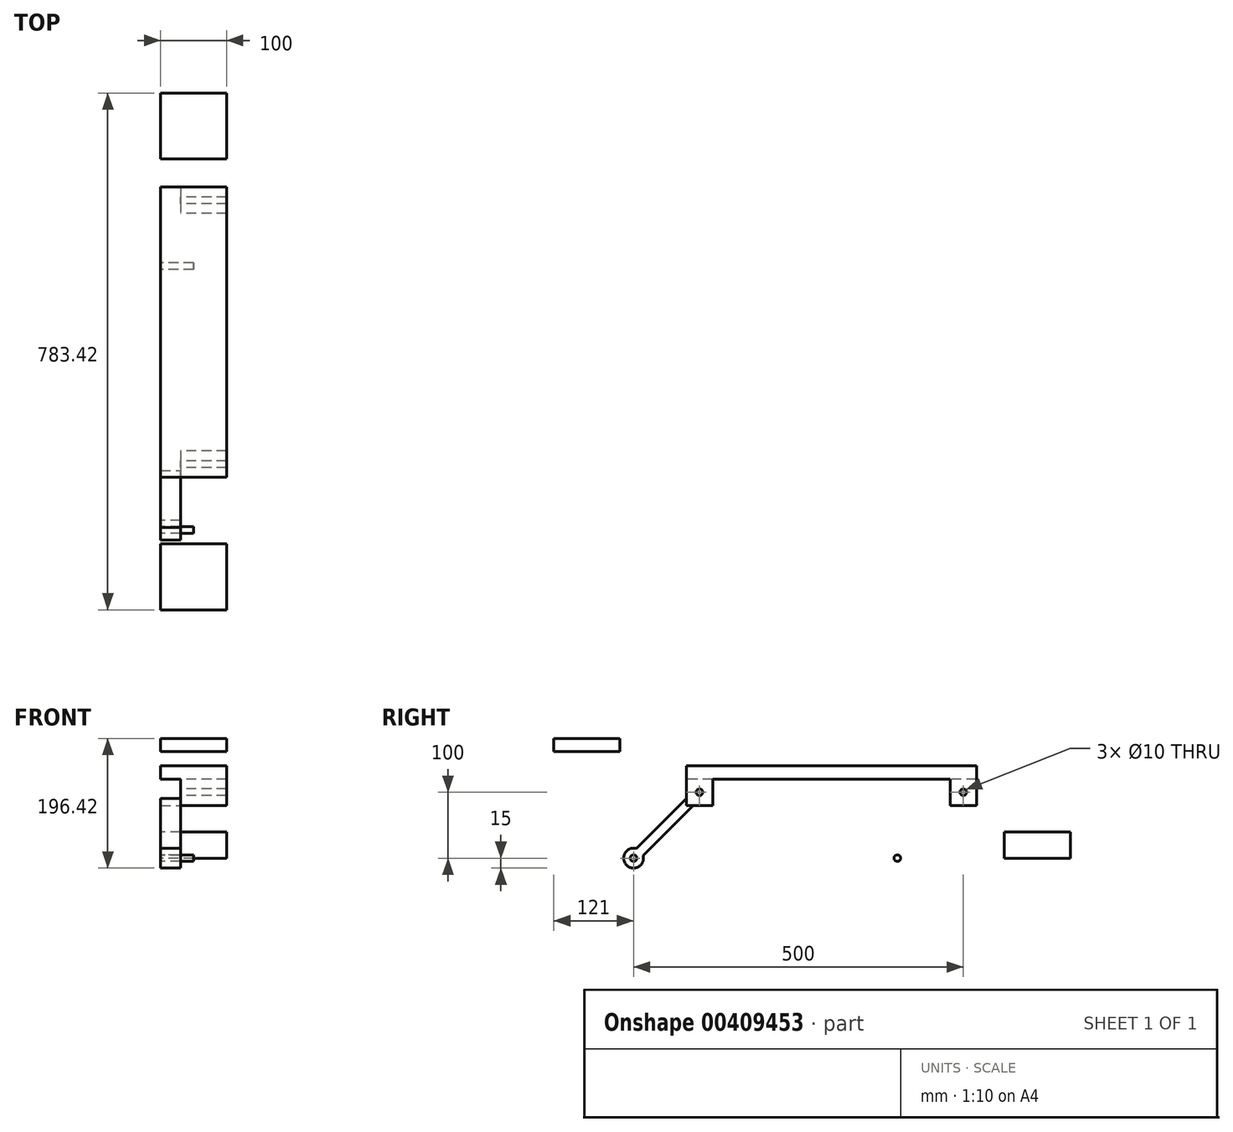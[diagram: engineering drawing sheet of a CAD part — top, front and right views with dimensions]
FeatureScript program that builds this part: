
annotation { "Feature Type Name" : "Feature", "Feature Type Description" : "" }
export const myFeature = defineFeature(function(context is Context, id is Id, definition is map)
    precondition{}
    {
        {
            var Q0;
            Q0=qCreatedBy(makeId("Right.planeOp"),FACE);
            var sketch = newSketch(context, id + "F0", { "sketchPlane" : qUnion([Q0])});
            skLineSegment(sketch, "E0", {"start": v(0, 0) * mm, "end": v(100, 100) * mm, "construction": true});
            skLineSegment(sketch, "E1", {"start": v(100, 100) * mm, "end": v(500, 100) * mm, "construction": true});
            skLineSegment(sketch, "E2", {"start": v(500, 100) * mm, "end": v(400, 0) * mm, "construction": true});
            skLineSegment(sketch, "E3", {"start": v(400, 0) * mm, "end": v(0, 0) * mm, "construction": true});
            skCircle(sketch, "E4", {"center": v(100, 100) * mm, "radius": 5 * mm});
            skCircle(sketch, "E5", {"center": v(500, 100) * mm, "radius": 5 * mm});
            skLineSegment(sketch, "E6.bottom", {"start": v(120, 80) * mm, "end": v(80, 80) * mm});
            skLineSegment(sketch, "E6.top", {"start": v(120, 120) * mm, "end": v(80, 120) * mm});
            skLineSegment(sketch, "E6.left", {"start": v(120, 80) * mm, "end": v(120, 120) * mm});
            skLineSegment(sketch, "E6.right", {"start": v(80, 80) * mm, "end": v(80, 120) * mm});
            skLineSegment(sketch, "E7.bottom", {"start": v(520, 80) * mm, "end": v(480, 80) * mm});
            skLineSegment(sketch, "E7.top", {"start": v(520, 120) * mm, "end": v(480, 120) * mm});
            skLineSegment(sketch, "E7.left", {"start": v(520, 80) * mm, "end": v(520, 120) * mm});
            skLineSegment(sketch, "E7.right", {"start": v(480, 80) * mm, "end": v(480, 120) * mm});
            skLineSegment(sketch, "E8.bottom", {"start": v(80, 120) * mm, "end": v(520, 120) * mm});
            skLineSegment(sketch, "E8.top", {"start": v(80, 140) * mm, "end": v(520, 140) * mm});
            skLineSegment(sketch, "E8.left", {"start": v(80, 120) * mm, "end": v(80, 140) * mm});
            skLineSegment(sketch, "E8.right", {"start": v(520, 120) * mm, "end": v(520, 140) * mm});
            skCircle(sketch, "E9", {"center": v(100, 100) * mm, "radius": 15 * mm});
            skCircle(sketch, "E10", {"center": v(0, 0) * mm, "radius": 15 * mm});
            skLineSegment(sketch, "E11", {"start": v(3.88, 14.49) * mm, "end": v(85.51, 96.12) * mm});
            skLineSegment(sketch, "E12.MirrorCS", {"start": v(14.49, 3.88) * mm, "end": v(96.12, 85.51) * mm});
            skCircle(sketch, "E13", {"center": v(0, 0) * mm, "radius": 5 * mm});
            skCircle(sketch, "E14", {"center": v(400, 0) * mm, "radius": 141.42 * mm, "construction": true});
            skLineSegment(sketch, "E15", {"start": v(400, 0) * mm, "end": v(949.52, 0) * mm, "construction": true});
            skLineSegment(sketch, "E16.bottom", {"start": v(562.42, 0) * mm, "end": v(662.42, 0) * mm});
            skLineSegment(sketch, "E16.top", {"start": v(562.42, 40) * mm, "end": v(662.42, 40) * mm});
            skLineSegment(sketch, "E16.left", {"start": v(562.42, 0) * mm, "end": v(562.42, 40) * mm});
            skLineSegment(sketch, "E16.right", {"start": v(662.42, 0) * mm, "end": v(662.42, 40) * mm});
            skCircle(sketch, "E17", {"center": v(0, 0) * mm, "radius": 141.42 * mm, "construction": true});
            skLineSegment(sketch, "E18", {"start": v(0, 0) * mm, "end": v(0, 382.71) * mm, "construction": true});
            skLineSegment(sketch, "E19.bottom", {"start": v(-21, 181.42) * mm, "end": v(-121, 181.42) * mm});
            skLineSegment(sketch, "E19.top", {"start": v(-21, 161.42) * mm, "end": v(-121, 161.42) * mm});
            skLineSegment(sketch, "E19.left", {"start": v(-21, 181.42) * mm, "end": v(-21, 161.42) * mm});
            skLineSegment(sketch, "E19.right", {"start": v(-121, 181.42) * mm, "end": v(-121, 161.42) * mm});
            skCircle(sketch, "E20", {"center": v(400, 0) * mm, "radius": 5 * mm});
            skSolve(sketch);
        }
        {
            var Q0;
            {var subQ1=sQuery(id+"F0.wireOp",EDGE,"E6.left");Q0=makeQuery(id+"F0.imprint","IMPRINT",FACE,{"disambiguationData":[TD([[makeQuery(id+"F0.imprint","IMPRINT",EDGE,{"derivedFrom":subQ1}),1.0]])]});}
            var Q1;
            {var subQ3=sQuery(id+"F0.wireOp",EDGE,"E6.right");var subQ7=sQuery(id+"F0.wireOp",EDGE,"E6.bottom");var subQ8=makeQuery(id+"F0.imprint","INTERSECT",VERTEX,{"derivedFrom":[subQ7,subQ3]});Q1=makeQuery(id+"F0.imprint","IMPRINT",FACE,{"disambiguationData":[TD([[makeQuery(id+"F0.imprint","IMPRINT",EDGE,{"disambiguationData":[TD([[subQ8,1.0]])],"derivedFrom":subQ7}),-1.0]])]});}
            var Q2;
            Q2=makeQuery(id+"F0.imprint","IMPRINT",FACE,{"disambiguationData":[TD([[makeQuery(id+"F0.imprint","IMPRINT",EDGE,{"derivedFrom":sQuery(id+"F0.wireOp",EDGE,"E4")}),-1.0]])]});
            var Q3;
            Q3=makeQuery(id+"F0.imprint","IMPRINT",FACE,{"disambiguationData":[TD([[makeQuery(id+"F0.imprint","IMPRINT",EDGE,{"derivedFrom":sQuery(id+"F0.wireOp",EDGE,"E8.top")}),-1.0]])]});
            var Q4;
            Q4=makeQuery(id+"F0.imprint","IMPRINT",FACE,{"disambiguationData":[TD([[makeQuery(id+"F0.imprint","IMPRINT",EDGE,{"derivedFrom":sQuery(id+"F0.wireOp",EDGE,"E5")}),-1.0]])]});
            extrude(context, id + "F1", {"entities" : qUnion([Q0, Q1, Q2, Q3, Q4]), "depth" : 100 * mm});
        }
        {
            var Q0;
            Q0=makeQuery(id+"F0.imprint","IMPRINT",FACE,{"disambiguationData":[TD([[makeQuery(id+"F0.imprint","IMPRINT",EDGE,{"derivedFrom":sQuery(id+"F0.wireOp",EDGE,"E4")}),-1.0]])]});
            var Q1;
            {var subQ3=sQuery(id+"F0.wireOp",EDGE,"E6.right");var subQ7=sQuery(id+"F0.wireOp",EDGE,"E6.bottom");var subQ8=makeQuery(id+"F0.imprint","INTERSECT",VERTEX,{"derivedFrom":[subQ7,subQ3]});Q1=makeQuery(id+"F0.imprint","IMPRINT",FACE,{"disambiguationData":[TD([[makeQuery(id+"F0.imprint","IMPRINT",EDGE,{"disambiguationData":[TD([[subQ8,1.0]])],"derivedFrom":subQ7}),-1.0]])]});}
            var Q2;
            {var subQ3=sQuery(id+"F0.wireOp",EDGE,"E6.right");var subQ5=sQuery(id+"F0.wireOp",EDGE,"E6.bottom");var subQ6=makeQuery(id+"F0.imprint","INTERSECT",VERTEX,{"derivedFrom":[subQ5,subQ3]});Q2=makeQuery(id+"F0.imprint","IMPRINT",FACE,{"disambiguationData":[TD([[makeQuery(id+"F0.imprint","IMPRINT",EDGE,{"disambiguationData":[TD([[subQ6,1.0]])],"derivedFrom":subQ5}),1.0]])]});}
            var Q3;
            Q3=makeQuery(id+"F0.imprint","IMPRINT",FACE,{"disambiguationData":[TD([[makeQuery(id+"F0.imprint","IMPRINT",EDGE,{"derivedFrom":sQuery(id+"F0.wireOp",EDGE,"E13")}),-1.0]])]});
            extrude(context, id + "F2", {"entities" : qUnion([Q0, Q1, Q2, Q3]), "depth" : 30 * mm});
        }
        {
            var Q0;
            {var subQ1=sQuery(id+"F0.wireOp",EDGE,"E6.left");Q0=makeQuery(id+"F0.imprint","IMPRINT",FACE,{"disambiguationData":[TD([[makeQuery(id+"F0.imprint","IMPRINT",EDGE,{"derivedFrom":subQ1}),1.0]])]});}
            var Q1;
            Q1=makeQuery(id+"F0.imprint","IMPRINT",FACE,{"disambiguationData":[TD([[makeQuery(id+"F0.imprint","IMPRINT",EDGE,{"derivedFrom":sQuery(id+"F0.wireOp",EDGE,"E4")}),-1.0]])]});
            var Q2;
            {var subQ3=sQuery(id+"F0.wireOp",EDGE,"E6.right");var subQ7=sQuery(id+"F0.wireOp",EDGE,"E6.bottom");var subQ8=makeQuery(id+"F0.imprint","INTERSECT",VERTEX,{"derivedFrom":[subQ7,subQ3]});Q2=makeQuery(id+"F0.imprint","IMPRINT",FACE,{"disambiguationData":[TD([[makeQuery(id+"F0.imprint","IMPRINT",EDGE,{"disambiguationData":[TD([[subQ8,1.0]])],"derivedFrom":subQ7}),-1.0]])]});}
            var Q3;
            Q3=makeQuery(id+"F0.imprint","IMPRINT",FACE,{"disambiguationData":[TD([[makeQuery(id+"F0.imprint","IMPRINT",EDGE,{"derivedFrom":sQuery(id+"F0.wireOp",EDGE,"E5")}),-1.0]])]});
            extrude(context, id + "F3", {"entities" : qUnion([Q0, Q1, Q2, Q3]), "operationType" : NewBodyOperationType.REMOVE, "depth" : 30 * mm});
        }
        {
            var Q0;
            Q0=makeQuery(id+"F0.imprint","IMPRINT",FACE,{"disambiguationData":[TD([[makeQuery(id+"F0.imprint","IMPRINT",EDGE,{"derivedFrom":sQuery(id+"F0.wireOp",EDGE,"E16.bottom")}),1.0]])]});
            extrude(context, id + "F4", {"entities" : qUnion([Q0]), "depth" : 100 * mm});
        }
        {
            var Q0;
            Q0=makeQuery(id+"F0.imprint","IMPRINT",FACE,{"disambiguationData":[TD([[makeQuery(id+"F0.imprint","IMPRINT",EDGE,{"derivedFrom":sQuery(id+"F0.wireOp",EDGE,"E19.bottom")}),1.0]])]});
            extrude(context, id + "F5", {"entities" : qUnion([Q0]), "depth" : 100 * mm});
        }
        {
            var Q0;
            Q0=makeQuery(id+"F0.imprint","IMPRINT",FACE,{"disambiguationData":[TD([[makeQuery(id+"F0.imprint","IMPRINT",EDGE,{"derivedFrom":sQuery(id+"F0.wireOp",EDGE,"E13")}),1.0]])]});
            var Q1;
            Q1=makeQuery(id+"F0.imprint","IMPRINT",FACE,{"disambiguationData":[TD([[makeQuery(id+"F0.imprint","IMPRINT",EDGE,{"derivedFrom":sQuery(id+"F0.wireOp",EDGE,"E20")}),1.0]])]});
            extrude(context, id + "F6", {"entities" : qUnion([Q0, Q1]), "depth" : 50 * mm});
        }
    });
